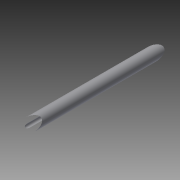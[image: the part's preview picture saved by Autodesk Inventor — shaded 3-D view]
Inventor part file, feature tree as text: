
AUTODESK INVENTOR PART (.ipt)
format: ipt  version: 2014 SP1 (Build 180222100, 222)  size: 86,528 bytes
history: native  units: in
note: dims shown in document units (in); Inventor stores cm internally (conversion verified against a paired STEP export)
features: extrude x1, fillet x1, sketch x1
ambient origin geometry x8: Origin, YZ Plane, XZ Plane, XY Plane, X Axis, Y Axis, Z Axis, Center Point
bodies: Solid1 (feature_tree)
feature tree (3):
  extrude  "Extrusion1"  Depth=1.0in
  fillet  "Fillet1"  Radius=31.75in
  sketch  "Sketch1"  dims[d0=2.5in d1=0.75in d2=31.75in d3=0.0in d4=1.0in]
